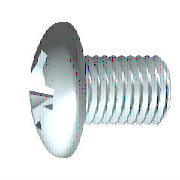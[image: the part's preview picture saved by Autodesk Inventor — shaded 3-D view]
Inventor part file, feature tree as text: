
AUTODESK INVENTOR PART (.ipt)
format: ipt  version: 2013 (Build 170138000, 138)  size: 330,240 bytes
history: native  units: mm (DEFAULTED — no unit token found)
features: extrude x2, other x1, plane x1
ambient origin geometry x7: Origin, YZ Plane, XZ Plane, X Axis, Y Axis, Z Axis, Center Point
bodies: Solid1 (feature_tree), Body (feature_tree)
feature tree (4):
  extrude  "Slot"  Depth=6.35mm
  other  "Cut"
  extrude  "Star Cut"  Depth=4.0386mm
  plane  "Work Plane3"
